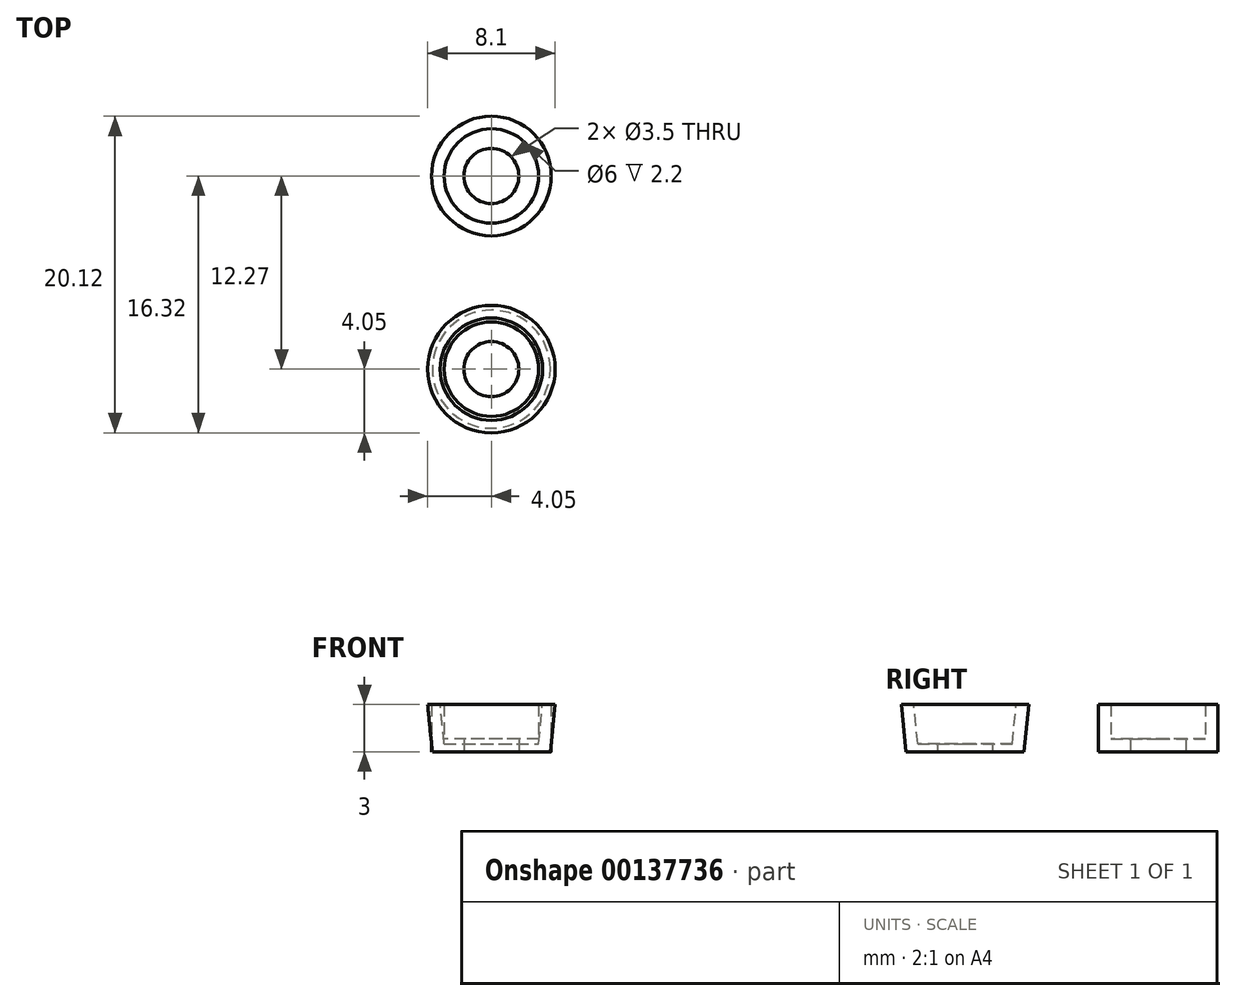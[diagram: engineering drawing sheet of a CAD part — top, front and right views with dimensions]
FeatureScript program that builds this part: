
annotation { "Feature Type Name" : "Feature", "Feature Type Description" : "" }
export const myFeature = defineFeature(function(context is Context, id is Id, definition is map)
    precondition{}
    {
        {
            var Q0;
            Q0=qCreatedBy(makeId("Top.planeOp"),FACE);
            var sketch = newSketch(context, id + "F0", { "sketchPlane" : qUnion([Q0])});
            skCircle(sketch, "E0", {"center": v(0, 0) * mm, "radius": 3.8 * mm});
            skCircle(sketch, "E1", {"center": v(0, 0) * mm, "radius": 1.75 * mm});
            skSolve(sketch);
        }
        {
            var Q0;
            Q0 = qSketchRegion(id + "F0", true);
            extrude(context, id + "F1", {"entities" : qUnion([Q0]), "depth" : 3 * mm});
        }
        {
            var Q0;
            Q0=makeQuery(id+"F1.opExtrude","CAP_FACE",FACE,{"disambiguationData":[OSD([sQuery(id+"F0.wireOp",EDGE,"E0"),sQuery(id+"F0.wireOp",EDGE,"E1")])],"isStart":false});
            var Q1;
            Q1=makeQuery(id+"F1.opExtrude","SWEPT_FACE",FACE,{"disambiguationData":[OSD([sQuery(id+"F0.wireOp",EDGE,"E1")])]});
            var Q2;
            Q2=makeQuery(id+"F1.opExtrude","SWEPT_BODY",BODY,{"disambiguationData":[OSD([sQuery(id+"F0.wireOp",EDGE,"E0"),sQuery(id+"F0.wireOp",EDGE,"E1")])]});
            shell(context, id + "F2", {"entities" : qUnion([Q0, Q1]), "parts" : qUnion([Q2]), "thickness" : .8 * mm});
        }
        {
            var Q0;
            Q0=qCreatedBy(makeId("Right.planeOp"),FACE);
            var sketch = newSketch(context, id + "F3", { "sketchPlane" : qUnion([Q0])});
            skLineSegment(sketch, "E2", {"start": v(-12.27, 0) * mm, "end": v(-14.02, 0) * mm, "construction": true});
            skLineSegment(sketch, "E3", {"start": v(-14.02, 0) * mm, "end": v(-15.22, 0) * mm});
            skLineSegment(sketch, "E4", {"start": v(-15.22, 0) * mm, "end": v(-16.02, 0) * mm});
            skLineSegment(sketch, "E5", {"start": v(-16.02, 0) * mm, "end": v(-16.32, 3) * mm});
            skLineSegment(sketch, "E6", {"start": v(-16.32, 3) * mm, "end": v(-15.52, 3) * mm});
            skLineSegment(sketch, "E7", {"start": v(-15.52, 3) * mm, "end": v(-15.27, 0.5) * mm});
            skLineSegment(sketch, "E8", {"start": v(-15.27, 0.5) * mm, "end": v(-14.02, 0.5) * mm});
            skLineSegment(sketch, "E9", {"start": v(-14.02, 0.5) * mm, "end": v(-14.02, 0) * mm});
            skLineSegment(sketch, "E10", {"start": v(-15.27, 0.5) * mm, "end": v(-16.07, 0.5) * mm, "construction": true});
            skLineSegment(sketch, "E11", {"start": v(-12.27, -1.26) * mm, "end": v(-12.27, 5.69) * mm, "construction": true});
            skSolve(sketch);
        }
        {
            var Q0;
            Q0 = qSketchRegion(id + "F3", true);
            var Q1;
            Q1=sQuery(id+"F3.wireOp",EDGE,"E11");
            revolve(context, id + "F4", {"entities" : qUnion([Q0]), "axis" : qUnion([Q1]), "revolveType" : RevolveType.FULL});
        }
    });
